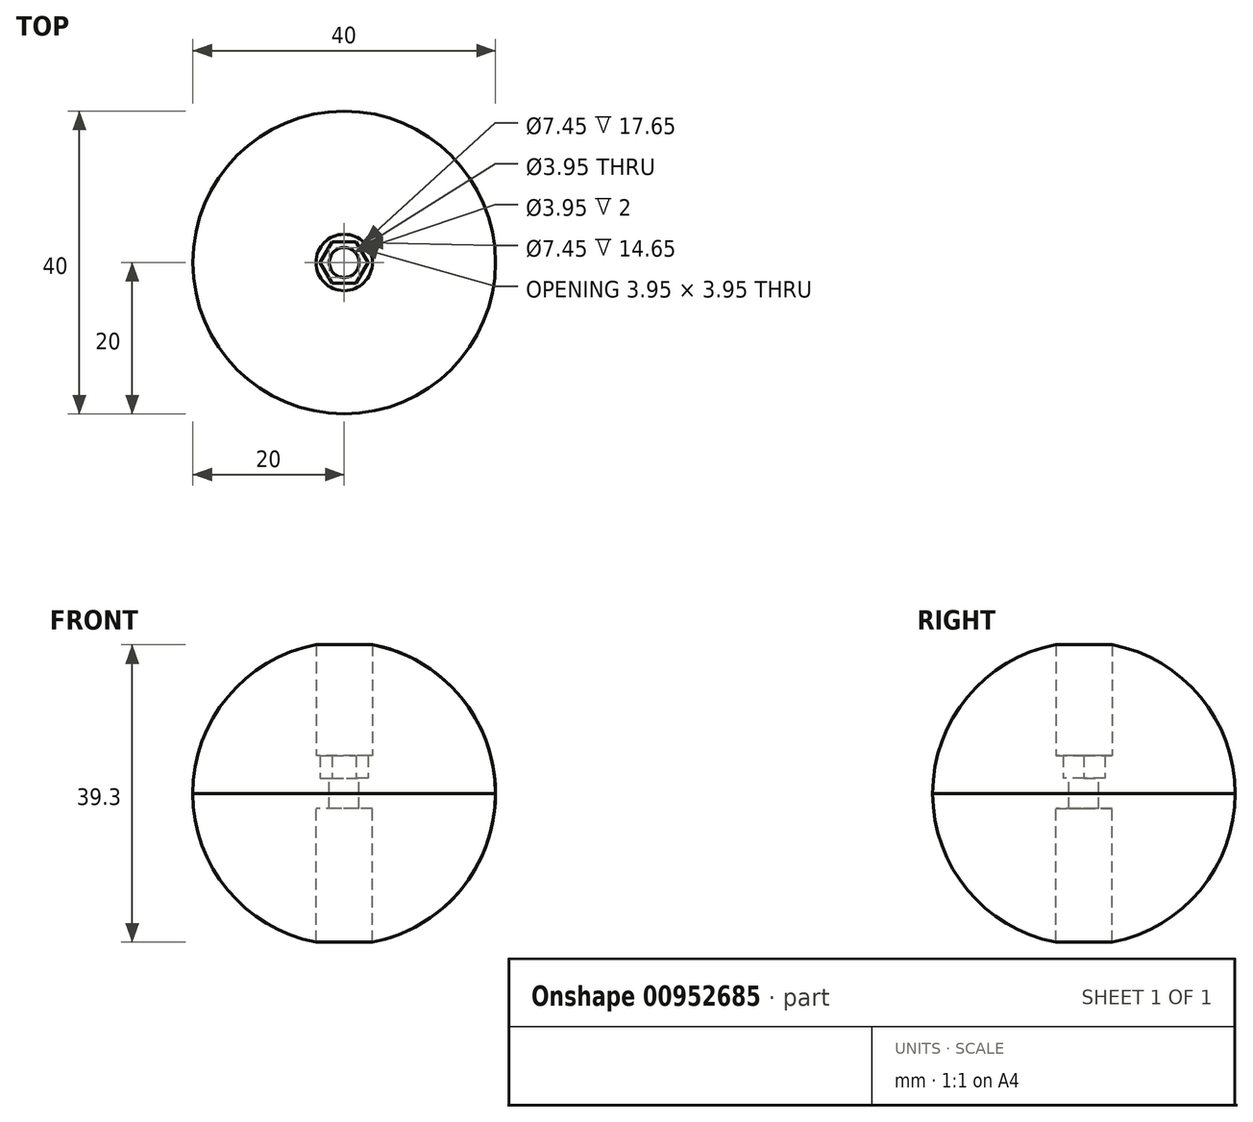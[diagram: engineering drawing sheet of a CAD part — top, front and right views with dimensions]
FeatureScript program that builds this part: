
annotation { "Feature Type Name" : "Feature", "Feature Type Description" : "" }
export const myFeature = defineFeature(function(context is Context, id is Id, definition is map)
    precondition{}
    {
        {
            var Q0;
            Q0=qCreatedBy(makeId("Front.planeOp"),FACE);
            var sketch = newSketch(context, id + "F0", { "sketchPlane" : qUnion([Q0])});
            skCircle(sketch, "E0", {"center": v(0, 0) * mm, "radius": 20 * mm});
            skLineSegment(sketch, "E1", {"start": v(24.84, 0) * mm, "end": v(-26.05, 0) * mm});
            skLineSegment(sketch, "E2", {"start": v(0, 20) * mm, "end": v(0, -20) * mm});
            skSolve(sketch);
        }
        {
            var Q0;
            {var subQ0=sQuery(id+"F0.wireOp",EDGE,"E2");var subQ1=sQuery(id+"F0.wireOp",EDGE,"E0");var subQ2=makeQuery(id+"F0.imprint","INTERSECT",VERTEX,{"disambiguationData":[OD(0.0)],"derivedFrom":[subQ1,subQ0]});Q0=makeQuery(id+"F0.imprint","IMPRINT",FACE,{"disambiguationData":[TD([[makeQuery(id+"F0.imprint","IMPRINT",EDGE,{"disambiguationData":[TD([[subQ2,-1.0]])],"derivedFrom":subQ1}),1.0]])]});}
            var Q1;
            Q1=sQuery(id+"F0.wireOp",EDGE,"E2");
            revolve(context, id + "F1", {"surfaceOperationType" : NewSurfaceOperationType.NEW, "entities" : qUnion([Q0]), "axis" : qUnion([Q1]), "revolveType" : RevolveType.FULL});
        }
        {
            var Q0;
            {var subQ0=sQuery(id+"F0.wireOp",EDGE,"E2");var subQ1=sQuery(id+"F0.wireOp",EDGE,"E0");var subQ2=makeQuery(id+"F0.imprint","INTERSECT",VERTEX,{"disambiguationData":[OD(1.0)],"derivedFrom":[subQ1,subQ0]});Q0=makeQuery(id+"F0.imprint","IMPRINT",FACE,{"disambiguationData":[TD([[makeQuery(id+"F0.imprint","IMPRINT",EDGE,{"disambiguationData":[TD([[subQ2,-1.0]])],"derivedFrom":subQ1}),1.0]])]});}
            var Q1;
            Q1=sQuery(id+"F0.wireOp",EDGE,"E2");
            revolve(context, id + "F2", {"surfaceOperationType" : NewSurfaceOperationType.NEW, "entities" : qUnion([Q0]), "axis" : qUnion([Q1]), "revolveType" : RevolveType.FULL});
        }
        {
            var Q0;
            Q0=makeQuery(id+"F1.opRevolve","SWEPT_FACE",FACE,{"disambiguationData":[OSD([sQuery(id+"F0.wireOp",EDGE,"E1")])]});
            var sketch = newSketch(context, id + "F3", { "sketchPlane" : qUnion([Q0])});
            skCircle(sketch, "E3.cCircle", {"center": v(0, 0) * mm, "radius": 2.75 * mm, "construction": true});
            skLineSegment(sketch, "E3.0", {"start": v(-1.59, 2.75) * mm, "end": v(1.59, 2.75) * mm});
            skLineSegment(sketch, "E3.1", {"start": v(1.59, 2.75) * mm, "end": v(3.18, 0) * mm});
            skLineSegment(sketch, "E3.2", {"start": v(3.18, 0) * mm, "end": v(1.59, -2.75) * mm});
            skLineSegment(sketch, "E3.3", {"start": v(1.59, -2.75) * mm, "end": v(-1.59, -2.75) * mm});
            skLineSegment(sketch, "E3.4", {"start": v(-1.59, -2.75) * mm, "end": v(-3.18, 0) * mm});
            skLineSegment(sketch, "E3.5", {"start": v(-3.18, 0) * mm, "end": v(-1.59, 2.75) * mm});
            skPoint(sketch, "E3.0.midPoint", {"position": v(0, 2.75) * mm});
            skSolve(sketch);
        }
        {
            var Q0;
            Q0=makeQuery(id+"F3.imprint","IMPRINT",FACE,{"disambiguationData":[TD([[makeQuery(id+"F3.imprint","IMPRINT",EDGE,{"derivedFrom":sQuery(id+"F3.wireOp",EDGE,"E3.0")}),-1.0]])]});
            extrude(context, id + "F4", {"entities" : qUnion([Q0]), "operationType" : NewBodyOperationType.REMOVE, "oppositeDirection" : true, "depth" : 25 * mm, "offsetDistance" : 25 * mm, "hasSecondDirection" : true, "secondDirectionOppositeDirection" : true, "secondDirectionDepth" : 2 * mm});
        }
        {
            var Q0;
            Q0=makeQuery(id+"F2.opRevolve","SWEPT_FACE",FACE,{"disambiguationData":[OSD([sQuery(id+"F0.wireOp",EDGE,"E1")])]});
            var sketch = newSketch(context, id + "F5", { "sketchPlane" : qUnion([Q0])});
            skCircle(sketch, "E4", {"center": v(0, 0) * mm, "radius": 3.73 * mm});
            skSolve(sketch);
        }
        {
            var Q0;
            Q0=makeQuery(id+"F5.imprint","IMPRINT",FACE,{"disambiguationData":[TD([[makeQuery(id+"F5.imprint","IMPRINT",EDGE,{"derivedFrom":sQuery(id+"F5.wireOp",EDGE,"E4")}),1.0]])]});
            extrude(context, id + "F6", {"entities" : qUnion([Q0]), "operationType" : NewBodyOperationType.REMOVE, "oppositeDirection" : true, "depth" : 25 * mm, "offsetDistance" : 25 * mm, "hasSecondDirection" : true, "secondDirectionOppositeDirection" : true, "secondDirectionDepth" : 2 * mm});
        }
        {
            var Q0;
            Q0=qCreatedBy(makeId("Top.planeOp"),FACE);
            var sketch = newSketch(context, id + "F7", { "sketchPlane" : qUnion([Q0])});
            skCircle(sketch, "E5", {"center": v(0, 0) * mm, "radius": 1.98 * mm});
            skSolve(sketch);
        }
        {
            var Q0;
            Q0=makeQuery(id+"F7.imprint","IMPRINT",FACE,{"disambiguationData":[TD([[makeQuery(id+"F7.imprint","IMPRINT",EDGE,{"derivedFrom":sQuery(id+"F7.wireOp",EDGE,"E5")}),1.0]])]});
            extrude(context, id + "F8", {"entities" : qUnion([Q0]), "operationType" : NewBodyOperationType.REMOVE, "oppositeDirection" : true, "depth" : 25 * mm, "offsetDistance" : 25 * mm, "hasSecondDirection" : true, "secondDirectionOppositeDirection" : false, "secondDirectionDepth" : 25 * mm});
        }
        {
            var Q0;
            Q0=makeQuery(id+"F5.imprint","IMPRINT",FACE,{"disambiguationData":[TD([[makeQuery(id+"F5.imprint","IMPRINT",EDGE,{"derivedFrom":sQuery(id+"F5.wireOp",EDGE,"E4")}),1.0]])]});
            extrude(context, id + "F9", {"entities" : qUnion([Q0]), "operationType" : NewBodyOperationType.REMOVE, "depth" : 34.2 * mm, "offsetDistance" : 25 * mm, "hasSecondDirection" : true, "secondDirectionOppositeDirection" : false, "secondDirectionDepth" : 5 * mm});
        }
    });
